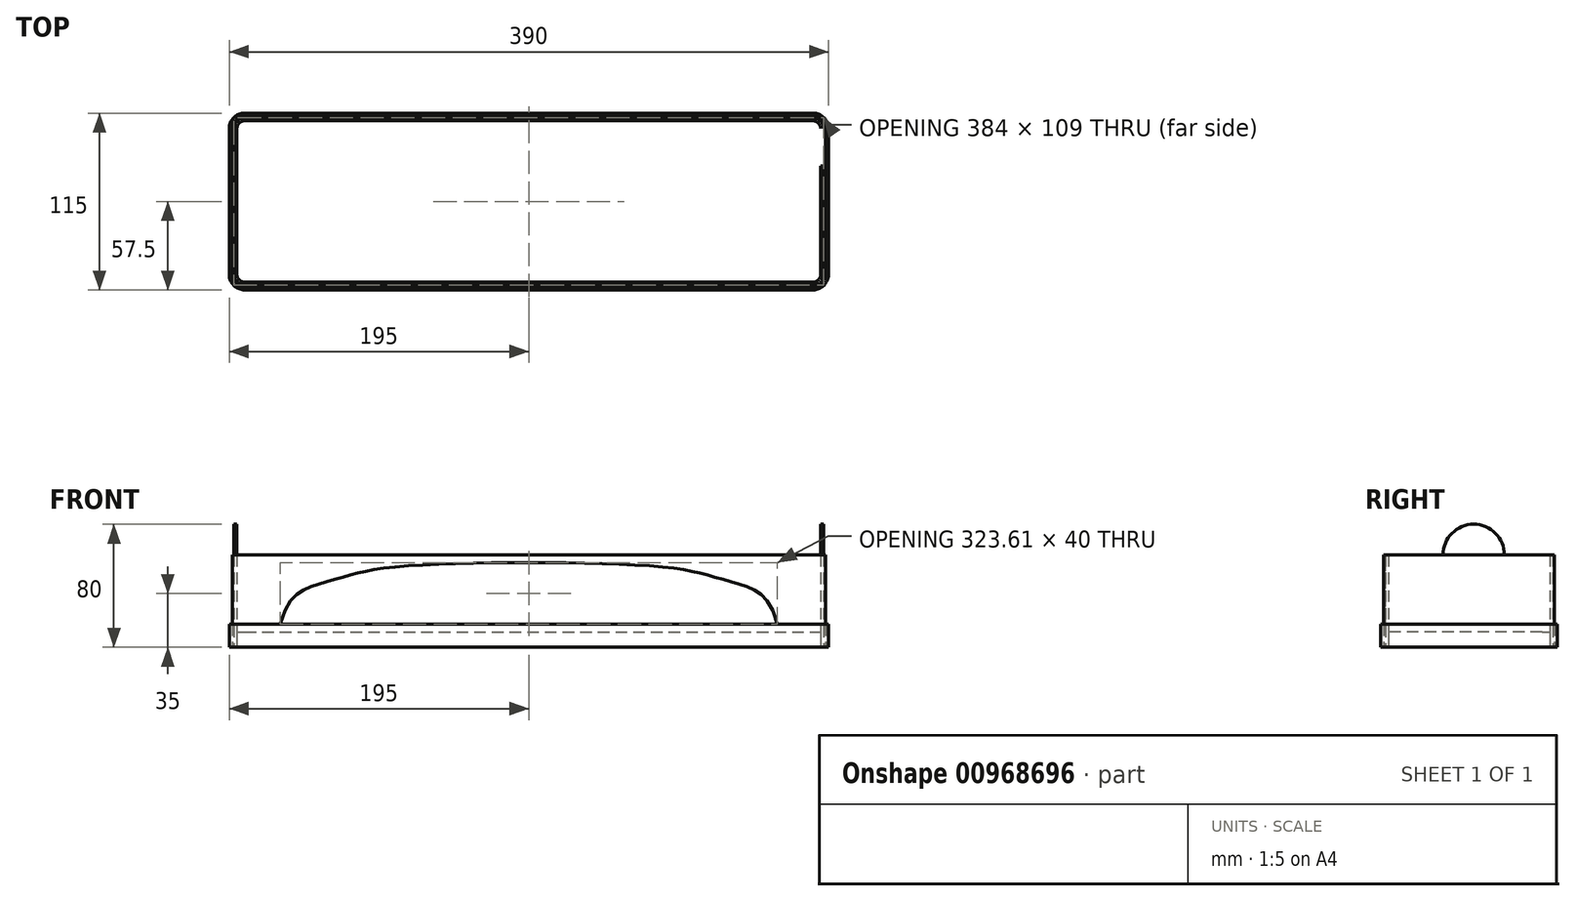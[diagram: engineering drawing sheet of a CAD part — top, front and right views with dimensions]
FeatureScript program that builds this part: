
annotation { "Feature Type Name" : "Feature", "Feature Type Description" : "" }
export const myFeature = defineFeature(function(context is Context, id is Id, definition is map)
    precondition{}
    {
        {
            var Q0;
            Q0=qCreatedBy(makeId("Top.planeOp"),FACE);
            var sketch = newSketch(context, id + "F0", { "sketchPlane" : qUnion([Q0])});
            skLineSegment(sketch, "E0.bottom", {"start": v(5, 105) * mm, "end": v(375, 105) * mm});
            skLineSegment(sketch, "E0.top", {"start": v(5, 0) * mm, "end": v(375, 0) * mm});
            skLineSegment(sketch, "E0.left", {"start": v(0, 100) * mm, "end": v(0, 5) * mm});
            skLineSegment(sketch, "E0.right", {"start": v(380, 100) * mm, "end": v(380, 5) * mm});
            skPoint(sketch, "E1.visualSharp", {"position": v(0, 105) * mm});
            skArc(sketch, "E1.filletArc", {"start": v(5, 105) * mm, "mid": v(1.46, 103.54) * mm, "end": v(0, 100) * mm});
            skPoint(sketch, "E2.visualSharp", {"position": v(0, 0) * mm});
            skArc(sketch, "E2.filletArc", {"start": v(0, 5) * mm, "mid": v(1.46, 1.46) * mm, "end": v(5, 0) * mm});
            skPoint(sketch, "E3.visualSharp", {"position": v(380, 0) * mm});
            skArc(sketch, "E3.filletArc", {"start": v(375, 0) * mm, "mid": v(378.54, 1.46) * mm, "end": v(380, 5) * mm});
            skPoint(sketch, "E4.visualSharp", {"position": v(380, 105) * mm});
            skArc(sketch, "E4.filletArc", {"start": v(380, 100) * mm, "mid": v(378.54, 103.54) * mm, "end": v(375, 105) * mm});
            skSolve(sketch);
        }
        {
            var Q0;
            Q0=qCreatedBy(makeId("Top.planeOp"),FACE);
            var sketch = newSketch(context, id + "F1", { "sketchPlane" : qUnion([Q0])});
            skLineSegment(sketch, "E5.bottom", {"start": v(5, 105) * mm, "end": v(375, 105) * mm});
            skLineSegment(sketch, "E5.top", {"start": v(5, 0) * mm, "end": v(375, 0) * mm});
            skLineSegment(sketch, "E5.left", {"start": v(0, 100) * mm, "end": v(0, 5) * mm});
            skLineSegment(sketch, "E5.right", {"start": v(380, 100) * mm, "end": v(380, 5) * mm});
            skPoint(sketch, "E6.visualSharp", {"position": v(0, 105) * mm});
            skArc(sketch, "E6.filletArc", {"start": v(5, 105) * mm, "mid": v(1.46, 103.54) * mm, "end": v(0, 100) * mm});
            skPoint(sketch, "E7.visualSharp", {"position": v(0, 0) * mm});
            skArc(sketch, "E7.filletArc", {"start": v(0, 5) * mm, "mid": v(1.46, 1.46) * mm, "end": v(5, 0) * mm});
            skPoint(sketch, "E8.visualSharp", {"position": v(380, 0) * mm});
            skArc(sketch, "E8.filletArc", {"start": v(375, 0) * mm, "mid": v(378.54, 1.46) * mm, "end": v(380, 5) * mm});
            skPoint(sketch, "E9.visualSharp", {"position": v(380, 105) * mm});
            skArc(sketch, "E9.filletArc", {"start": v(380, 100) * mm, "mid": v(378.54, 103.54) * mm, "end": v(375, 105) * mm});
            skArc(sketch, "E10.0", {"start": v(-2, 5) * mm, "mid": v(0.05, 0.05) * mm, "end": v(5, -2) * mm});
            skLineSegment(sketch, "E10.1", {"start": v(-2, 100) * mm, "end": v(-2, 5) * mm});
            skLineSegment(sketch, "E10.2", {"start": v(5, -2) * mm, "end": v(375, -2) * mm});
            skArc(sketch, "E10.3", {"start": v(5, 107) * mm, "mid": v(0.05, 104.95) * mm, "end": v(-2, 100) * mm});
            skArc(sketch, "E10.4", {"start": v(375, -2) * mm, "mid": v(379.95, 0.05) * mm, "end": v(382, 5) * mm});
            skLineSegment(sketch, "E10.5", {"start": v(382, 100) * mm, "end": v(382, 5) * mm});
            skArc(sketch, "E10.6", {"start": v(382, 100) * mm, "mid": v(379.95, 104.95) * mm, "end": v(375, 107) * mm});
            skLineSegment(sketch, "E10.7", {"start": v(5, 107) * mm, "end": v(375, 107) * mm});
            skSolve(sketch);
        }
        {
            var Q0;
            Q0 = qSketchRegion(id + "F0", true);
            extrude(context, id + "F2", {"entities" : qUnion([Q0]), "depth" : 10 * mm, "offsetDistance" : 25 * mm});
        }
        {
            var Q0;
            Q0 = qSketchRegion(id + "F1", true);
            extrude(context, id + "F3", {"entities" : qUnion([Q0]), "depth" : 60 * mm, "offsetDistance" : 25 * mm});
        }
        {
            var Q0;
            Q0=makeQuery(id+"F3.opExtrude","SWEPT_FACE",FACE,{"disambiguationData":[OSD([sQuery(id+"F1.wireOp",EDGE,"E10.1")])]});
            var sketch = newSketch(context, id + "F4", { "sketchPlane" : qUnion([Q0])});
            skArc(sketch, "E11", {"start": v(-35.5, 60) * mm, "mid": v(-55.5, 80) * mm, "end": v(-75.5, 60) * mm});
            skLineSegment(sketch, "E12", {"start": v(-75.5, 60) * mm, "end": v(-35.5, 60) * mm});
            skSolve(sketch);
        }
        {
            var Q0;
            Q0 = qSketchRegion(id + "F4", true);
            extrude(context, id + "F5", {"entities" : qUnion([Q0]), "operationType" : NewBodyOperationType.ADD, "oppositeDirection" : true, "depth" : 2 * mm, "offsetDistance" : 25 * mm});
        }
        {
            var Q0;
            Q0=makeQuery(id+"F3.opExtrude","SWEPT_FACE",FACE,{"disambiguationData":[OSD([sQuery(id+"F1.wireOp",EDGE,"E10.5")])]});
            var sketch = newSketch(context, id + "F6", { "sketchPlane" : qUnion([Q0])});
            skArc(sketch, "E13", {"start": v(75.5, 60) * mm, "mid": v(55.5, 80) * mm, "end": v(35.5, 60) * mm});
            skLineSegment(sketch, "E14", {"start": v(35.5, 60) * mm, "end": v(75.5, 60) * mm});
            skSolve(sketch);
        }
        {
            var Q0;
            Q0 = qSketchRegion(id + "F6", true);
            extrude(context, id + "F7", {"entities" : qUnion([Q0]), "oppositeDirection" : true, "depth" : 2 * mm, "offsetDistance" : 25 * mm});
        }
        {
            var Q0;
            Q0=makeQuery(id+"F2.opExtrude","CAP_FACE",FACE,{"disambiguationData":[OSD([sQuery(id+"F0.wireOp",EDGE,"E0.bottom"),sQuery(id+"F0.wireOp",EDGE,"E0.top"),sQuery(id+"F0.wireOp",EDGE,"E0.left"),sQuery(id+"F0.wireOp",EDGE,"E0.right"),sQuery(id+"F0.wireOp",EDGE,"E1.filletArc"),sQuery(id+"F0.wireOp",EDGE,"E2.filletArc"),sQuery(id+"F0.wireOp",EDGE,"E3.filletArc"),sQuery(id+"F0.wireOp",EDGE,"E4.filletArc")])],"isStart":true});
            var sketch = newSketch(context, id + "F8", { "sketchPlane" : qUnion([Q0])});
            skArc(sketch, "E15.0", {"start": v(-3, -5) * mm, "mid": v(-0.66, 0.66) * mm, "end": v(5, 3) * mm});
            skLineSegment(sketch, "E15.1", {"start": v(-3, -100) * mm, "end": v(-3, -5) * mm});
            skLineSegment(sketch, "E15.2", {"start": v(5, 3) * mm, "end": v(375, 3) * mm});
            skArc(sketch, "E15.3", {"start": v(5, -108) * mm, "mid": v(-0.66, -105.66) * mm, "end": v(-3, -100) * mm});
            skArc(sketch, "E15.4", {"start": v(375, 3) * mm, "mid": v(380.66, 0.66) * mm, "end": v(383, -5) * mm});
            skLineSegment(sketch, "E15.5", {"start": v(383, -100) * mm, "end": v(383, -5) * mm});
            skArc(sketch, "E15.6", {"start": v(383, -100) * mm, "mid": v(380.66, -105.66) * mm, "end": v(375, -108) * mm});
            skLineSegment(sketch, "E15.7", {"start": v(5, -108) * mm, "end": v(375, -108) * mm});
            skLineSegment(sketch, "E16.0", {"start": v(-2, -100) * mm, "end": v(-2, -5) * mm});
            skArc(sketch, "E16.1", {"start": v(5, -107) * mm, "mid": v(0.05, -104.95) * mm, "end": v(-2, -100) * mm});
            skArc(sketch, "E16.2", {"start": v(-2, -5) * mm, "mid": v(0.05, -0.05) * mm, "end": v(5, 2) * mm});
            skLineSegment(sketch, "E16.3", {"start": v(5, -107) * mm, "end": v(375, -107) * mm});
            skLineSegment(sketch, "E16.4", {"start": v(5, 2) * mm, "end": v(375, 2) * mm});
            skArc(sketch, "E16.5", {"start": v(375, 2) * mm, "mid": v(379.95, -0.05) * mm, "end": v(382, -5) * mm});
            skLineSegment(sketch, "E16.6", {"start": v(382, -100) * mm, "end": v(382, -5) * mm});
            skArc(sketch, "E16.7", {"start": v(382, -100) * mm, "mid": v(379.95, -104.95) * mm, "end": v(375, -107) * mm});
            skSolve(sketch);
        }
        {
            var Q0;
            Q0 = qSketchRegion(id + "F8", true);
            extrude(context, id + "F9", {"entities" : qUnion([Q0]), "oppositeDirection" : true, "depth" : 60 * mm, "offsetDistance" : 25 * mm});
        }
        {
            var Q0;
            Q0=makeQuery(id+"F2.opExtrude","CAP_FACE",FACE,{"disambiguationData":[OSD([sQuery(id+"F0.wireOp",EDGE,"E0.bottom"),sQuery(id+"F0.wireOp",EDGE,"E0.top"),sQuery(id+"F0.wireOp",EDGE,"E0.left"),sQuery(id+"F0.wireOp",EDGE,"E0.right"),sQuery(id+"F0.wireOp",EDGE,"E1.filletArc"),sQuery(id+"F0.wireOp",EDGE,"E2.filletArc"),sQuery(id+"F0.wireOp",EDGE,"E3.filletArc"),sQuery(id+"F0.wireOp",EDGE,"E4.filletArc")])],"isStart":true});
            var sketch = newSketch(context, id + "F10", { "sketchPlane" : qUnion([Q0])});
            skArc(sketch, "E17.0", {"start": v(-5, -5) * mm, "mid": v(-2.07, 2.07) * mm, "end": v(5, 5) * mm});
            skLineSegment(sketch, "E17.1", {"start": v(-5, -100) * mm, "end": v(-5, -5) * mm});
            skLineSegment(sketch, "E17.2", {"start": v(5, 5) * mm, "end": v(375, 5) * mm});
            skArc(sketch, "E17.3", {"start": v(5, -110) * mm, "mid": v(-2.07, -107.07) * mm, "end": v(-5, -100) * mm});
            skArc(sketch, "E17.4", {"start": v(375, 5) * mm, "mid": v(382.07, 2.07) * mm, "end": v(385, -5) * mm});
            skLineSegment(sketch, "E17.5", {"start": v(385, -100) * mm, "end": v(385, -5) * mm});
            skArc(sketch, "E17.6", {"start": v(385, -100) * mm, "mid": v(382.07, -107.07) * mm, "end": v(375, -110) * mm});
            skLineSegment(sketch, "E17.7", {"start": v(5, -110) * mm, "end": v(375, -110) * mm});
            skSolve(sketch);
        }
        {
            var Q0;
            Q0 = qSketchRegion(id + "F10", true);
            extrude(context, id + "F11", {"entities" : qUnion([Q0]), "oppositeDirection" : true, "depth" : 15 * mm, "offsetDistance" : 25 * mm});
        }
        {
            var Q0;
            Q0=makeQuery(id+"F9.opExtrude","SWEPT_FACE",FACE,{"disambiguationData":[OSD([sQuery(id+"F8.wireOp",EDGE,"E15.2")])]});
            var sketch = newSketch(context, id + "F12", { "sketchPlane" : qUnion([Q0])});
            skLineSegment(sketch, "E18", {"start": v(190, 60) * mm, "end": v(190, 0) * mm, "construction": true});
            skPoint(sketch, "E19", {"position": v(190, 0) * mm});
            skFitSpline(sketch, "E20", {"points": [v(28.2, 15) * mm, v(48.8, 39.57) * mm, v(71.95, 46.45) * mm, v(97.3, 51.61) * mm, v(190, 55) * mm], "startDerivative": vector(64.66, 238.61) * mm, "endDerivative": vector(281.4, 0) * mm});
            skLineSegment(sketch, "E21", {"start": v(190, 55) * mm, "end": v(190, 15) * mm});
            skLineSegment(sketch, "E22", {"start": v(190, 15) * mm, "end": v(28.2, 15) * mm});
            skFitSpline(sketch, "E23.MirrorCS", {"points": [v(351.8, 15) * mm, v(331.2, 39.57) * mm, v(308.05, 46.45) * mm, v(282.7, 51.61) * mm, v(190, 55) * mm], "startDerivative": vector(-64.66, 238.61) * mm, "endDerivative": vector(-281.4, 0) * mm});
            skLineSegment(sketch, "E24.MirrorCS", {"start": v(190, 15) * mm, "end": v(351.8, 15) * mm});
            skSolve(sketch);
        }
        {
            var Q0;
            Q0 = qSketchRegion(id + "F12", true);
            extrude(context, id + "F13", {"entities" : qUnion([Q0]), "operationType" : NewBodyOperationType.REMOVE, "surfaceOperationType" : NewSurfaceOperationType.ADD, "endBound" : BoundingType.SYMMETRIC, "oppositeDirection" : true, "depth" : 2 * mm, "offsetDistance" : 25 * mm});
        }
    });
